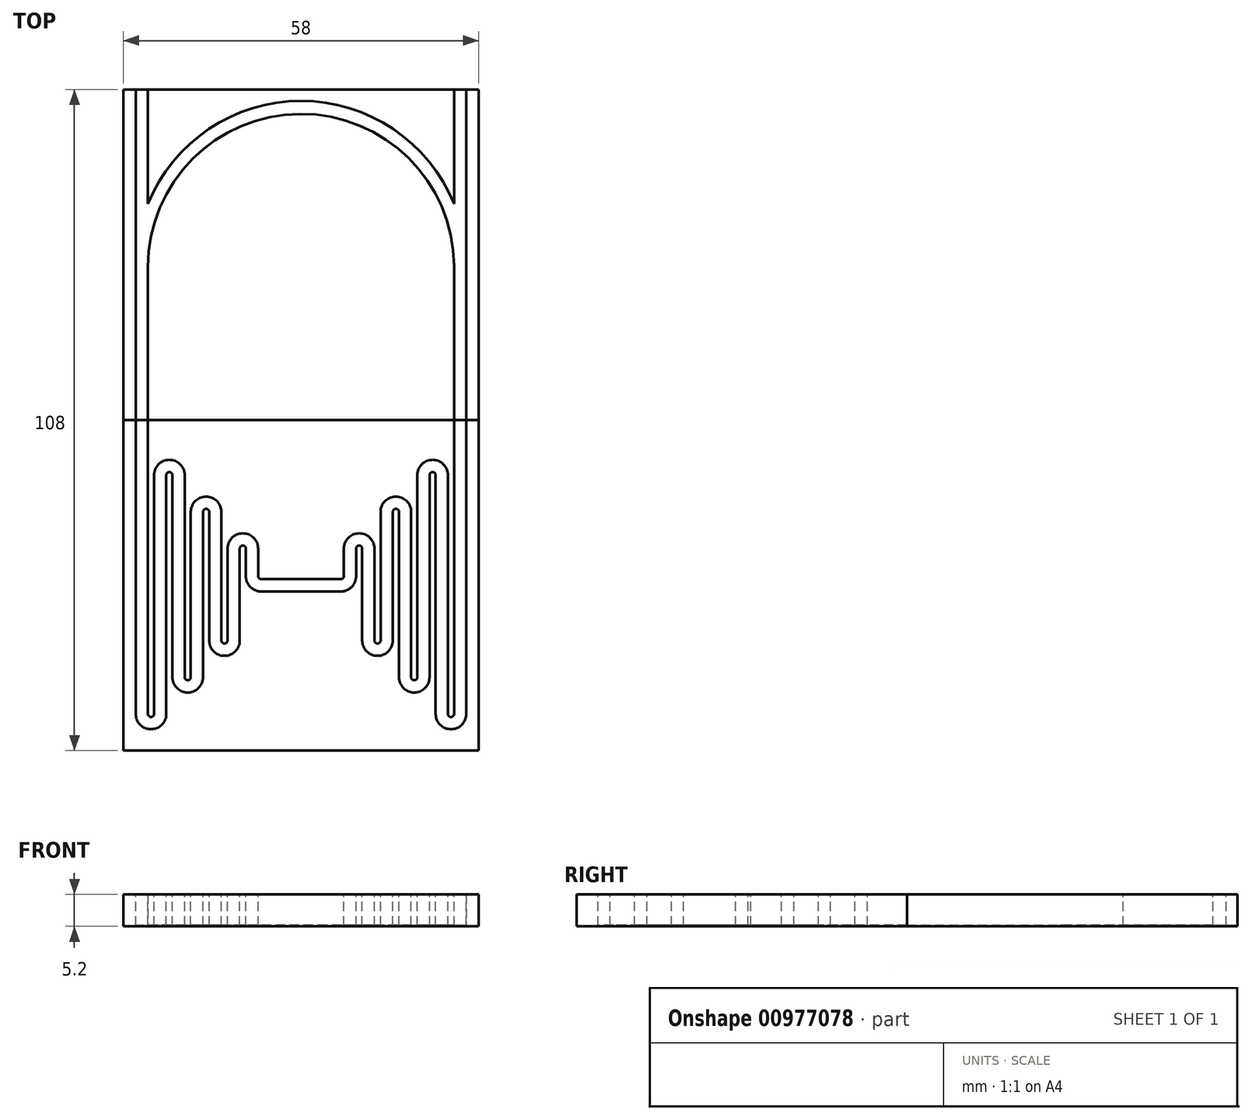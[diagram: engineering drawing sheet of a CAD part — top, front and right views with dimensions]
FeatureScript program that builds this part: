
annotation { "Feature Type Name" : "Feature", "Feature Type Description" : "" }
export const myFeature = defineFeature(function(context is Context, id is Id, definition is map)
    precondition{}
    {
        {
            var Q0;
            Q0=qCreatedBy(makeId("Top.planeOp"),FACE);
            var sketch = newSketch(context, id + "F0", { "sketchPlane" : qUnion([Q0])});
            skLineSegment(sketch, "E0.bottom", {"start": v(29, 27) * mm, "end": v(-29, 27) * mm});
            skLineSegment(sketch, "E0.top", {"start": v(29, -27) * mm, "end": v(-29, -27) * mm});
            skLineSegment(sketch, "E0.left", {"start": v(29, 27) * mm, "end": v(29, -27) * mm});
            skLineSegment(sketch, "E0.right", {"start": v(-29, 27) * mm, "end": v(-29, -27) * mm});
            skPoint(sketch, "E0.middle", {"position": v(0, 0) * mm});
            skSolve(sketch);
        }
        {
            var Q0;
            Q0=makeQuery(id+"F0.imprint","IMPRINT",FACE,{"disambiguationData":[TD([[makeQuery(id+"F0.imprint","IMPRINT",EDGE,{"derivedFrom":sQuery(id+"F0.wireOp",EDGE,"E0.bottom")}),1.0]])]});
            extrude(context, id + "F1", {"entities" : qUnion([Q0]), "depth" : 5.2 * mm, "offsetDistance" : 25 * mm});
        }
        {
            var Q0;
            Q0=makeQuery(id+"F1.opExtrude","CAP_FACE",FACE,{"disambiguationData":[OSD([sQuery(id+"F0.wireOp",EDGE,"E0.bottom"),sQuery(id+"F0.wireOp",EDGE,"E0.top"),sQuery(id+"F0.wireOp",EDGE,"E0.left"),sQuery(id+"F0.wireOp",EDGE,"E0.right")])],"isStart":false});
            var sketch = newSketch(context, id + "F2", { "sketchPlane" : qUnion([Q0])});
            skPoint(sketch, "E1.middle", {"position": v(-28, 0) * mm});
            skLineSegment(sketch, "E2.left", {"start": v(-27, 25) * mm, "end": v(-27, -21) * mm});
            skLineSegment(sketch, "E2.right", {"start": v(-25, 23.27) * mm, "end": v(-25, -21) * mm});
            skLineSegment(sketch, "E3.left", {"start": v(-25, 18) * mm, "end": v(-25, -21) * mm});
            skLineSegment(sketch, "E3.right", {"start": v(-24, 18) * mm, "end": v(-24, -21) * mm});
            skLineSegment(sketch, "E4.right", {"start": v(-22, 18) * mm, "end": v(-22, -21) * mm});
            skLineSegment(sketch, "E5.left", {"start": v(-21, 18) * mm, "end": v(-21, -15) * mm});
            skLineSegment(sketch, "E5.right", {"start": v(-19, 18) * mm, "end": v(-19, -15) * mm});
            skLineSegment(sketch, "E6.left", {"start": v(-18, 12) * mm, "end": v(-18, -15) * mm});
            skLineSegment(sketch, "E6.right", {"start": v(-16, 12) * mm, "end": v(-16, -15) * mm});
            skLineSegment(sketch, "E7.left", {"start": v(-15, 12) * mm, "end": v(-15, -9) * mm});
            skLineSegment(sketch, "E7.right", {"start": v(-13, 12) * mm, "end": v(-13, -9) * mm});
            skLineSegment(sketch, "E8.left", {"start": v(-12, 6) * mm, "end": v(-12, -9) * mm});
            skLineSegment(sketch, "E8.right", {"start": v(-10, 6) * mm, "end": v(-10, -9) * mm});
            skPoint(sketch, "E9.firstSnap0", {"position": v(-13, 1.5) * mm});
            skLineSegment(sketch, "E10.left", {"start": v(-9, 6) * mm, "end": v(-9, 1.5) * mm});
            skLineSegment(sketch, "E10.right", {"start": v(-7, 6) * mm, "end": v(-7, 1.5) * mm});
            skLineSegment(sketch, "E11.bottom", {"start": v(6.5, 1) * mm, "end": v(-6.5, 1) * mm});
            skLineSegment(sketch, "E11.top", {"start": v(6.5, -1) * mm, "end": v(-6.5, -1) * mm});
            skPoint(sketch, "E11.middle", {"position": v(0, 0) * mm});
            skArc(sketch, "E12", {"start": v(-9, 6) * mm, "mid": v(-9.5, 6.5) * mm, "end": v(-10, 6) * mm});
            skArc(sketch, "E13", {"start": v(-7, 6) * mm, "mid": v(-9.5, 8.5) * mm, "end": v(-12, 6) * mm});
            skArc(sketch, "E14", {"start": v(-13, -9) * mm, "mid": v(-12.5, -9.5) * mm, "end": v(-12, -9) * mm});
            skArc(sketch, "E15", {"start": v(-15, -9) * mm, "mid": v(-12.5, -11.5) * mm, "end": v(-10, -9) * mm});
            skArc(sketch, "E16", {"start": v(-15, 12) * mm, "mid": v(-15.5, 12.5) * mm, "end": v(-16, 12) * mm});
            skArc(sketch, "E17", {"start": v(-13, 12) * mm, "mid": v(-15.5, 14.5) * mm, "end": v(-18, 12) * mm});
            skArc(sketch, "E18", {"start": v(-19, -15) * mm, "mid": v(-18.5, -15.5) * mm, "end": v(-18, -15) * mm});
            skArc(sketch, "E19", {"start": v(-21, -15) * mm, "mid": v(-18.5, -17.5) * mm, "end": v(-16, -15) * mm});
            skArc(sketch, "E20", {"start": v(-21, 18) * mm, "mid": v(-21.5, 18.5) * mm, "end": v(-22, 18) * mm});
            skArc(sketch, "E21", {"start": v(-19, 18) * mm, "mid": v(-21.5, 20.5) * mm, "end": v(-24, 18) * mm});
            skArc(sketch, "E22", {"start": v(-25, -21) * mm, "mid": v(-24.5, -21.5) * mm, "end": v(-24, -21) * mm});
            skArc(sketch, "E23", {"start": v(-27, -21) * mm, "mid": v(-24.5, -23.5) * mm, "end": v(-22, -21) * mm});
            skArc(sketch, "E24", {"start": v(-7, 1.5) * mm, "mid": v(-6.86, 1.14) * mm, "end": v(-6.5, 1) * mm});
            skArc(sketch, "E25", {"start": v(-9, 1.5) * mm, "mid": v(-8.27, -0.27) * mm, "end": v(-6.5, -1) * mm});
            skLineSegment(sketch, "E26.left", {"start": v(25, 25) * mm, "end": v(25, -21) * mm});
            skLineSegment(sketch, "E26.right", {"start": v(27, 23.27) * mm, "end": v(27, -21) * mm});
            skLineSegment(sketch, "E27.right", {"start": v(25, 23.27) * mm, "end": v(25, -22.73) * mm});
            skLineSegment(sketch, "E28.left", {"start": v(22, 18) * mm, "end": v(22, -21) * mm});
            skLineSegment(sketch, "E28.right", {"start": v(24, 18) * mm, "end": v(24, -21) * mm});
            skLineSegment(sketch, "E29.left", {"start": v(19, 18) * mm, "end": v(19, -15) * mm});
            skLineSegment(sketch, "E29.right", {"start": v(21, 18) * mm, "end": v(21, -15) * mm});
            skLineSegment(sketch, "E30.left", {"start": v(16, 12) * mm, "end": v(16, -15) * mm});
            skLineSegment(sketch, "E30.right", {"start": v(18, 12) * mm, "end": v(18, -15) * mm});
            skLineSegment(sketch, "E31.right", {"start": v(16, 12) * mm, "end": v(16, -16.73) * mm});
            skLineSegment(sketch, "E32.left", {"start": v(13, 12) * mm, "end": v(13, -9) * mm});
            skLineSegment(sketch, "E32.right", {"start": v(15, 12) * mm, "end": v(15, -9) * mm});
            skLineSegment(sketch, "E33.left", {"start": v(10, 6) * mm, "end": v(10, -9) * mm});
            skLineSegment(sketch, "E33.right", {"start": v(12, 6) * mm, "end": v(12, -9) * mm});
            skLineSegment(sketch, "E34.left", {"start": v(7, 6) * mm, "end": v(7, 1.5) * mm});
            skLineSegment(sketch, "E34.right", {"start": v(9, 6) * mm, "end": v(9, 1.5) * mm});
            skArc(sketch, "E35", {"start": v(6.5, 1) * mm, "mid": v(6.85, 1.14) * mm, "end": v(7, 1.5) * mm});
            skArc(sketch, "E36", {"start": v(6.5, -1) * mm, "mid": v(8.26, -0.27) * mm, "end": v(9, 1.5) * mm});
            skArc(sketch, "E37", {"start": v(22, -21) * mm, "mid": v(24.5, -23.5) * mm, "end": v(27, -21) * mm});
            skArc(sketch, "E38", {"start": v(24, -21) * mm, "mid": v(24.5, -21.5) * mm, "end": v(25, -21) * mm});
            skArc(sketch, "E39", {"start": v(18, -15) * mm, "mid": v(18.5, -15.5) * mm, "end": v(19, -15) * mm});
            skArc(sketch, "E40", {"start": v(16, -15) * mm, "mid": v(18.5, -17.5) * mm, "end": v(21, -15) * mm});
            skArc(sketch, "E41", {"start": v(12, -9) * mm, "mid": v(12.5, -9.5) * mm, "end": v(13, -9) * mm});
            skArc(sketch, "E42", {"start": v(10, -9) * mm, "mid": v(12.5, -11.5) * mm, "end": v(15, -9) * mm});
            skArc(sketch, "E43", {"start": v(22, 18) * mm, "mid": v(21.5, 18.5) * mm, "end": v(21, 18) * mm});
            skArc(sketch, "E44", {"start": v(24, 18) * mm, "mid": v(21.5, 20.5) * mm, "end": v(19, 18) * mm});
            skArc(sketch, "E45", {"start": v(16, 12) * mm, "mid": v(15.5, 12.5) * mm, "end": v(15, 12) * mm});
            skArc(sketch, "E46", {"start": v(18, 12) * mm, "mid": v(15.5, 14.5) * mm, "end": v(13, 12) * mm});
            skArc(sketch, "E47", {"start": v(10, 6) * mm, "mid": v(9.5, 6.5) * mm, "end": v(9, 6) * mm});
            skArc(sketch, "E48", {"start": v(12, 6) * mm, "mid": v(9.5, 8.5) * mm, "end": v(7, 6) * mm});
            skLineSegment(sketch, "E49.top", {"start": v(-27, 27) * mm, "end": v(-25, 27) * mm});
            skLineSegment(sketch, "E49.left", {"start": v(-27, 25) * mm, "end": v(-27, 27) * mm});
            skLineSegment(sketch, "E49.right", {"start": v(-25, 25) * mm, "end": v(-25, 27) * mm});
            skLineSegment(sketch, "E50.top", {"start": v(25, 27) * mm, "end": v(27, 27) * mm});
            skLineSegment(sketch, "E50.left", {"start": v(25, 23.27) * mm, "end": v(25, 27) * mm});
            skLineSegment(sketch, "E50.right", {"start": v(27, 25) * mm, "end": v(27, 27) * mm});
            skLineSegment(sketch, "E51", {"start": v(27, 25) * mm, "end": v(27, 23.27) * mm});
            skLineSegment(sketch, "E52", {"start": v(-25, 25) * mm, "end": v(-25, 23.27) * mm});
            skSolve(sketch);
        }
        {
            var Q0;
            Q0=makeQuery(id+"F2.imprint","IMPRINT",FACE,{"disambiguationData":[TD([[makeQuery(id+"F2.imprint","IMPRINT",EDGE,{"derivedFrom":sQuery(id+"F2.wireOp",EDGE,"E2.left")}),1.0]])]});
            extrude(context, id + "F3", {"entities" : qUnion([Q0]), "operationType" : NewBodyOperationType.REMOVE, "oppositeDirection" : true, "depth" : 5 * mm, "offsetDistance" : 25 * mm});
        }
        {
            var Q0;
            Q0=qCreatedBy(makeId("Top.planeOp"),FACE);
            var sketch = newSketch(context, id + "F4", { "sketchPlane" : qUnion([Q0])});
            skLineSegment(sketch, "E53.bottom", {"start": v(-29, 27) * mm, "end": v(29, 27) * mm});
            skLineSegment(sketch, "E53.top", {"start": v(-29, 81) * mm, "end": v(29, 81) * mm});
            skLineSegment(sketch, "E53.left", {"start": v(-29, 27) * mm, "end": v(-29, 81) * mm});
            skLineSegment(sketch, "E53.right", {"start": v(29, 27) * mm, "end": v(29, 81) * mm});
            skSolve(sketch);
        }
        {
            var Q0;
            Q0=makeQuery(id+"F4.imprint","IMPRINT",FACE,{"disambiguationData":[TD([[makeQuery(id+"F4.imprint","IMPRINT",EDGE,{"derivedFrom":sQuery(id+"F4.wireOp",EDGE,"E53.bottom")}),1.0]])]});
            extrude(context, id + "F5", {"entities" : qUnion([Q0]), "depth" : 5.2 * mm, "offsetDistance" : 25 * mm});
        }
        {
            var Q0;
            Q0=makeQuery(id+"F5.opExtrude","CAP_FACE",FACE,{"disambiguationData":[OSD([sQuery(id+"F4.wireOp",EDGE,"E53.bottom"),sQuery(id+"F4.wireOp",EDGE,"E53.top"),sQuery(id+"F4.wireOp",EDGE,"E53.left"),sQuery(id+"F4.wireOp",EDGE,"E53.right")])],"isStart":false});
            var sketch = newSketch(context, id + "F6", { "sketchPlane" : qUnion([Q0])});
            skLineSegment(sketch, "E54.bottom", {"start": v(-27, 27) * mm, "end": v(-25, 27) * mm});
            skLineSegment(sketch, "E54.top", {"start": v(-27, 81) * mm, "end": v(-25, 81) * mm});
            skLineSegment(sketch, "E54.left", {"start": v(-27, 27) * mm, "end": v(-27, 81) * mm});
            skLineSegment(sketch, "E54.right", {"start": v(-25, 27) * mm, "end": v(-25, 81) * mm});
            skLineSegment(sketch, "E55.bottom", {"start": v(27, 27) * mm, "end": v(25, 27) * mm});
            skLineSegment(sketch, "E55.top", {"start": v(27, 81) * mm, "end": v(25, 81) * mm});
            skLineSegment(sketch, "E55.left", {"start": v(27, 27) * mm, "end": v(27, 81) * mm});
            skLineSegment(sketch, "E55.right", {"start": v(25, 27) * mm, "end": v(25, 81) * mm});
            skLineSegment(sketch, "E56.left", {"start": v(-25, 27) * mm, "end": v(-25, 52) * mm});
            skArc(sketch, "E57", {"start": v(25, 52) * mm, "mid": v(0, 77) * mm, "end": v(-25, 52) * mm});
            skArc(sketch, "E58", {"start": v(27, 52) * mm, "mid": v(0, 79.13) * mm, "end": v(-27, 52) * mm});
            skPoint(sketch, "E58.startSnap0", {"position": v(27, 54) * mm});
            skSolve(sketch);
        }
        {
            var Q0;
            Q0 = qSketchRegion(id + "F6", true);
            extrude(context, id + "F7", {"entities" : qUnion([Q0]), "operationType" : NewBodyOperationType.REMOVE, "oppositeDirection" : true, "depth" : 5 * mm, "offsetDistance" : 25 * mm});
        }
    });
